# Revit family: Qmax 225(Shrd)
name_source: partatom
category: Plumbing Fixtures
revit_build: Autodesk Revit 2013 (Build: 20120221_2030(x64)
units: mm (PartAtom-declared; Revit-internal decimal feet)

## types (5) — shared parameters
150-225 Step Connector - Dimensions = Ø310mm x 25mm (ØxL)
150-225 Step Connector - Material = High Density Polyethylene
150-225 Step Connector - Model Description = High capacity slot drainage channel system
150-225 Step Connector - Product Code = 32995
150-225 Step Connector - Recyclable = Fully recyclable
150-225 Step Connector - Recycled Material Content = 0%
150-225 Step Connector - Weight = 0.4 kg
ACO Hydraulic Design Software = http://www.acodesign.co.uk
Assembly Code = D2040
Channel C.S.A = 39761mm²
Channel Colour = Black
Channel Material = Medium Density Polyethylene
Channel Recyclable = Fully recyclable
Channel Recycled Material Content = Variable %
Concrete Surround Volume - Load Class A 15 - E 600 = 0.255 m³/m
Concrete Surround Volume - Load Class F 900 = 0.345 m³/m
Edge Rail Recyclable = Fully recyclable
Edge Rail Recycled Material Content = Between 40% - 90%
Fax = +44 (0)1462 815895
Hydraulic Performance = http://www.aco.co.uk
Installation - Concrete Grade = Refer to brochure
Installation - Reinforcement Details = Refer to brochure
Installation Guidelines = http://www.aco.co.uk
Length = 2000 mm  [stored 6.56168 ft]
Load Class = A 15 - F 900
Maintenance Guidelines = http://www.aco.co.uk
Manufacturer = ACO Technologies plc - ACO Water Management Division
Model = ACO Qmax 225
Model Description = High capacity slot drainage channel system
Multi-Functional End Cap - Channel Material = Medium Density Polyethylene
Multi-Functional End Cap - Channel Recyclable = Fully recyclable
Multi-Functional End Cap - Channel Recycled Material Content = Variable %
Multi-Functional End Cap - Dimensions = Ø290mm x 240mm (ØxL)
Multi-Functional End Cap - Model Description = High capacity slot drainage channel system
Multi-Functional End Cap - Product Code = 42221
Multi-Functional End Cap - Seal Colour = Black
Multi-Functional End Cap - Seal Material = Chloroprene
Multi-Functional End Cap - Seal Recyclable = Fully recyclable
Multi-Functional End Cap - Seal Recycled Material Content = 0%
Multi-Functional End Cap - Weight = 1.4 kg
Price = POA - contact ACO
Product Brochure = http://www.aco.co.uk
Product Page URL = http://www.aco.co.uk
Product Standard = BS EN 1433:2002 CE marked
Revision = 1
Seal Colour = Black
Seal Material = Chloroprene
Seal Recyclable = Fully recyclable
Seal Recycled Material Content = 0%
Telephone = +44 (0)1462 816666
URL = www.aco.co.uk
Width Overall = 290 mm  [stored 0.951444 ft]
zero-valued in all types: Cost, SerialNumber, TagNumber

## per-type parameters (varying)
| type | 150-225 Step Connector - Colour | BoreCentre | Depth Overall | Drainage Slot Intake Area | Drainage Slot Width | E1-QFlow-DuctileIron | E2-QGuard-DuctileIron | E3-QFlow-GalvSteel | E4-QGuard-GalvSteel | E5-QSlot-GalvSteel | Edge Rail Colour | Edge Rail Finish | Edge Rail Material | Floor Opening Width | Invert Depth | Material | Multi-Functional End Cap - Channel Colour | Product Code | Product Dimensions | Product Weight | Type Comments | V_CoarseE1 | V_Coarse_E5 |
| 32800 - Q-Flow Edge - D.I | Black | 311.5 mm  [stored 1.02198 ft] | 480 mm  [stored 1.5748 ft] | 18775mm²/m | 26mm | Yes | No | No | No | No | Black | ATec coating | Ductile Iron | 65 mm  [stored 0.213255 ft] | 425mm | Iron, Ductile | Black | 32800 | 2000mm x 290mm x 480mm (LxWxH) | 24kg | ACO Qmax 225 channel assembly complete with ACO Q-Flow ductile iron edge rail | Yes | No |
| 32801 - Q-Guard Edge - D.I | Black
Medium Density Polyethylene | 311.5 mm  [stored 1.02198 ft] | 480 mm  [stored 1.5748 ft] | 10925mm²/m | 8mm twin slot | No | Yes | No | No | No | Black | ATec coating | Ductile Iron | 65 mm  [stored 0.213255 ft] | 425mm | Iron, Ductile | Black | 32801 | 2000mm x 290mm x 480mm (LxWxH) | 25 kg | ACO Qmax 225 channel assembly complete with ACO Q-Guard ductile iron edge rail | Yes | No |
| 32802 - Q-Flow Edge - G.S | Black
Medium Density Polyethylene | 311.5 mm  [stored 1.02198 ft] | 480 mm  [stored 1.5748 ft] | 18106mm²/m | 26mm | No | No | Yes | No | No | Silver
Silver | Galvanised | Steel | 90 mm  [stored 0.295276 ft] | 425mm | Steel, Galvanized | Black
Medium Density Polyethylene | 32802 | 2000mm x 290mm x 480mm (LxWxH) | 17.8 kg | ACO Qmax 225 channel assembly complete with ACO Q-Flow galvanised steel edge rail | Yes | No |
| 32803 - Q-Guard Edge - G.S | Black
Medium Density Polyethylene | 311.5 mm  [stored 1.02198 ft] | 480 mm  [stored 1.5748 ft] | 8356mm²/m | 10mm | No | No | No | Yes | No | Silver | Galvanised | Steel | 55 mm  [stored 0.180446 ft] | 425mm | Steel, Galvanized | Black
Medium Density Polyethylene | 32803 | 2000mm x 290mm x 480mm (LxWxH) | 15.3 kg | ACO Qmax 225 channel assembly complete with ACO Q-Guard galvanised steel edge rail | Yes | No |
| 32804 - Q-Slot Edge - G.S | Black
Medium Density Polyethylene | 411.5 mm  [stored 1.35007 ft] | 580 mm  [stored 1.90289 ft] | 10000mm²/m | 10mm | No | No | No | No | Yes | Silver | Galvanised | Steel | 18 mm  [stored 0.0590551 ft] | 525mm | Steel, Galvanized | Black
Medium Density Polyethylene | 32804 | 2000mm x 290mm x 580mm (LxWxH) | 22.9 kg | ACO Qmax 225 channel assembly complete with ACO Q-Slot galvanised steel edge rail | No | Yes |

note: [stored X ft] marks values corroborated as IEEE doubles in the binary element streams (Revit-internal decimal feet)

## geometry (parser evidence)
native form markers: Blend x4, Sweep x14
no freeform markers — native parametric forms only
